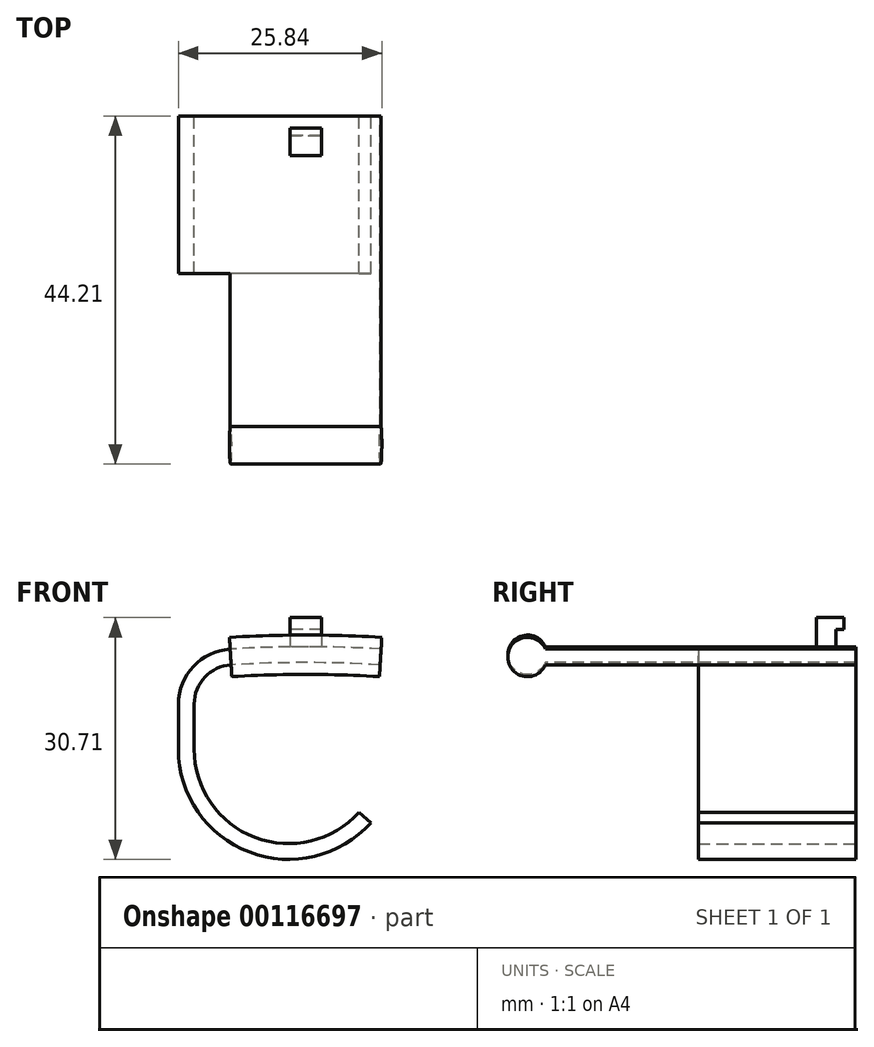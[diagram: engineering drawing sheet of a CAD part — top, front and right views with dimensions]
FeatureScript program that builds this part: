
annotation { "Feature Type Name" : "Feature", "Feature Type Description" : "" }
export const myFeature = defineFeature(function(context is Context, id is Id, definition is map)
    precondition{}
    {
        {
            var Q0;
            Q0=qCreatedBy(makeId("Front.planeOp"),FACE);
            var sketch = newSketch(context, id + "F0", { "sketchPlane" : qUnion([Q0])});
            skArc(sketch, "E0", {"start": v(-8, 155.8) * mm, "mid": v(-4, 155.95) * mm, "end": v(0, 156) * mm, "construction": true});
            skLineSegment(sketch, "E1", {"start": v(0, 156) * mm, "end": v(0, 0) * mm, "construction": true});
            skLineSegment(sketch, "E2", {"start": v(-8, 155.8) * mm, "end": v(0, 0) * mm, "construction": true});
            skArc(sketch, "E3.MirrorCS", {"start": v(8, 155.8) * mm, "mid": v(4, 155.95) * mm, "end": v(0, 156) * mm, "construction": true});
            skSolve(sketch);
        }
        {
            var Q0;
            Q0=qCreatedBy(makeId("Right.planeOp"),FACE);
            var sketch = newSketch(context, id + "F1", { "sketchPlane" : qUnion([Q0])});
            skArc(sketch, "E4", {"start": v(2.3, 157) * mm, "mid": v(-2.5, 156) * mm, "end": v(2.3, 155) * mm});
            skLineSegment(sketch, "E5.bottom", {"start": v(2.3, 155) * mm, "end": v(41.7, 155) * mm});
            skLineSegment(sketch, "E5.top", {"start": v(2.3, 157) * mm, "end": v(41.7, 157) * mm});
            skLineSegment(sketch, "E5.right", {"start": v(41.7, 157) * mm, "end": v(41.7, 155) * mm});
            skPoint(sketch, "E5.middle", {"position": v(22, 156) * mm});
            skLineSegment(sketch, "E6", {"start": v(-19.16, 0) * mm, "end": v(25.8, 0) * mm, "construction": true});
            skSolve(sketch);
        }
        {
            var Q0;
            Q0=makeQuery(id+"F1.imprint","IMPRINT",FACE,{"disambiguationData":[TD([[makeQuery(id+"F1.imprint","IMPRINT",EDGE,{"derivedFrom":sQuery(id+"F1.wireOp",EDGE,"E4")}),1.0]])]});
            var Q1;
            Q1=sQuery(id+"F1.wireOp",EDGE,"E6");
            revolve(context, id + "F2", {"entities" : qUnion([Q0]), "axis" : qUnion([Q1]), "revolveType" : RevolveType.SYMMETRIC, "angle" : 7 * degree});
        }
        {
            var Q0;
            Q0=makeQuery(id+"F2.opRevolve","SWEPT_FACE",FACE,{"disambiguationData":[OSD([sQuery(id+"F1.wireOp",EDGE,"E5.right")])]});
            var sketch = newSketch(context, id + "F3", { "sketchPlane" : qUnion([Q0])});
            skArc(sketch, "E7", {"start": v(14.16, 149.72) * mm, "mid": v(12.8, 153.15) * mm, "end": v(9.46, 154.71) * mm});
            skLineSegment(sketch, "E8", {"start": v(14.16, 149.72) * mm, "end": v(14.16, 144) * mm});
            skArc(sketch, "E9.filletArc", {"start": v(-6.79, 136) * mm, "mid": v(6.44, 132.79) * mm, "end": v(14.16, 144) * mm});
            skArc(sketch, "E10.0", {"start": v(16.16, 149.72) * mm, "mid": v(14.26, 154.52) * mm, "end": v(9.58, 156.7) * mm});
            skLineSegment(sketch, "E10.1", {"start": v(16.16, 149.72) * mm, "end": v(16.16, 144) * mm});
            skArc(sketch, "E10.2", {"start": v(-8.28, 134.67) * mm, "mid": v(7.15, 130.92) * mm, "end": v(16.16, 144) * mm});
            skLineSegment(sketch, "E11", {"start": v(9.46, 154.71) * mm, "end": v(9.58, 156.7) * mm});
            skLineSegment(sketch, "E12", {"start": v(-6.79, 136) * mm, "end": v(-8.28, 134.67) * mm});
            skLineSegment(sketch, "E13", {"start": v(2.16, 144) * mm, "end": v(-6.79, 136) * mm, "construction": true});
            skSolve(sketch);
        }
        {
            var Q0;
            Q0 = qSketchRegion(id + "F3", true);
            extrude(context, id + "F4", {"entities" : qUnion([Q0]), "operationType" : NewBodyOperationType.ADD, "oppositeDirection" : true, "depth" : 20 * mm});
        }
        {
            var Q0;
            Q0=qCreatedBy(makeId("Right.planeOp"),FACE);
            var sketch = newSketch(context, id + "F5", { "sketchPlane" : qUnion([Q0])});
            skLineSegment(sketch, "E14.bottom", {"start": v(36.7, 160.7) * mm, "end": v(39.2, 160.7) * mm});
            skLineSegment(sketch, "E14.top", {"start": v(36.7, 155.84) * mm, "end": v(39.2, 155.84) * mm});
            skLineSegment(sketch, "E14.left", {"start": v(36.7, 160.7) * mm, "end": v(36.7, 155.84) * mm});
            skLineSegment(sketch, "E14.right", {"start": v(39.2, 159.2) * mm, "end": v(39.2, 155.84) * mm});
            skLineSegment(sketch, "E15.bottom", {"start": v(39.2, 160.7) * mm, "end": v(40.2, 160.7) * mm});
            skLineSegment(sketch, "E15.top", {"start": v(39.2, 159.2) * mm, "end": v(40.2, 159.2) * mm});
            skLineSegment(sketch, "E15.right", {"start": v(40.2, 160.7) * mm, "end": v(40.2, 159.2) * mm});
            skSolve(sketch);
        }
        {
            var Q0;
            Q0 = qSketchRegion(id + "F5", true);
            extrude(context, id + "F6", {"entities" : qUnion([Q0]), "operationType" : NewBodyOperationType.ADD, "endBound" : BoundingType.SYMMETRIC, "depth" : 4 * mm});
        }
    });
